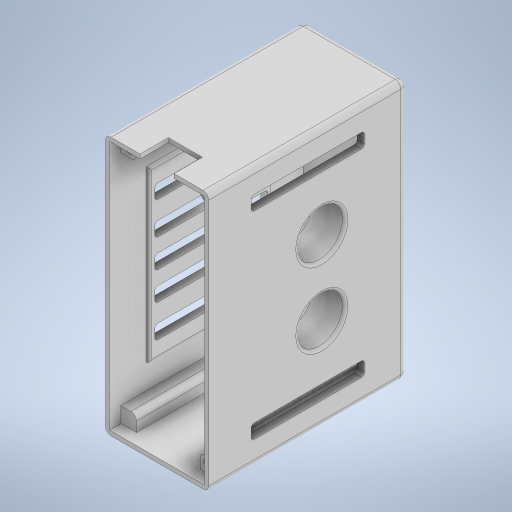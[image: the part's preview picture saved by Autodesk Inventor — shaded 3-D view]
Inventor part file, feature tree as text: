
AUTODESK INVENTOR PART (.ipt)
format: ipt  version: 2024 (Build 280153000, 153)  size: 593,920 bytes
history: native  units: mm
features: extrude x13, sketch x13, fillet x11
ambient origin geometry x8: Origin, YZ Plane, XZ Plane, XY Plane, X Axis, Y Axis, Z Axis, Center Point
bodies: Volumenkörper1 (feature_tree)
feature tree (37):
  extrude  "Extrusion1"  Depth=36.6mm
  extrude  "Extrusion2"  Depth=1.5mm
  extrude  "Extrusion3"  Depth=1.5mm
  extrude  "Extrusion5"  Depth=68.5mm TaperAngle=0.0deg
  fillet  "Rundung2"  Radius=30.0mm
  extrude  "Extrusion9"  Depth=16.5mm
  extrude  "Extrusion11"  Depth=2.0mm TaperAngle=0.0deg
  extrude  "Extrusion12"  Depth=18.0mm
  sketch  "Skizze15"  dims[d50=5.5mm d51=5.5mm d55=5.5mm]
  sketch  "Skizze16"  dims[d56=5.5mm d57=5.5mm]
  fillet  "Rundung5"  Radius=11.0mm
  fillet  "Rundung6"  Radius=1.0mm
  extrude  "Extrusion17"  Depth=5.5mm
  sketch  "Skizze24"  dims[d71=2.5mm d72=15.0mm d73=0.0mm d74=10.0mm d75=12.0mm d76=4.0mm d77=0.0mm d85=11.5mm d86=10.0mm]
  fillet  "Rundung7"  Radius=5.5mm
  extrude  "Extrusion21"  Depth=5.5mm
  extrude  "Extrusion23"  Depth=2.5mm
  extrude  "Extrusion24"  Depth=15.0mm TaperAngle=0.0deg
  fillet  "Rundung8"  Radius=10.0mm
  fillet  "Rundung9"  Radius=12.0mm
  fillet  "Rundung10"  Radius=4.0mm
  fillet  "Rundung11"  Radius=11.5mm
  fillet  "Rundung12"  Radius=10.0mm
  extrude  "Extrusion26"  Depth=5.0mm
  fillet  "Rundung13"  Radius=5.0mm
  extrude  "Extrusion27"  Depth=5.0mm
  fillet  "Rundung14"  Radius=5.0mm
  sketch  "Skizze1"  dims[d0=91.5mm d1=36.6mm]
  sketch  "Skizze2"  dims[d2=70.0mm d3=0.0mm d4=1.5mm]
  sketch  "Skizze3"  dims[d5=1.5mm d6=1.5mm]
  sketch  "Skizze5"  dims[d7=1.5mm d8=68.5mm d9=0.0mm d10=30.0mm]
  sketch  "Skizze10"  dims[d11=16.5mm d12=16.5mm]
  sketch  "Skizze13"  dims[d13=26.5mm d14=2.0mm d15=0.0mm]
  sketch  "Skizze14"  dims[d18=18.0mm d19=18.0mm d20=11.0mm d21=0.0mm d49=1.0mm]
  sketch  "Skizze19"  dims[d58=64.5mm d59=0.0mm d70=2.5mm]
  sketch  "Skizze28"  dims[d87=11.5mm d88=5.0mm d89=5.0mm]
  sketch  "Skizze30"  dims[d90=5.0mm d91=5.0mm d92=5.0mm d93=40.0mm d94=10.0mm d98=5.0mm d99=5.0mm d100=40.0mm d101=70.0mm d105=2.0mm d106=2.0mm d111=45.0mm d112=20.5mm d114=12.0mm d116=5.0mm d118=5.0mm d119=5.0mm d120=5.0mm d121=12.0mm d122=16.5mm d123=2.0mm d124=11.0mm d125=0.0mm d126=9.25mm d127=3.1mm d128=3.1mm d129=3.1mm d130=3.1mm d149=1.5mm d150=1.5mm d151=1.5mm d152=1.5mm d153=1.5mm d154=1.5mm d155=1.5mm d156=1.5mm d157=1.5mm d158=1.5mm d159=1.5mm d160=1.5mm d161=1.0mm d162=5.0mm d163=0.0mm d175=22.0mm d176=30.0mm d177=1.0mm d178=0.0mm d179=7.0mm d180=0.0mm d181=1.0mm d182=1.0mm d183=1.0mm d184=1.0mm d185=1.0mm d190=7.5mm d191=44.0mm d192=44.0mm d193=13.0mm d194=1.0mm d195=0.0mm d196=1.0mm d197=3.0mm d198=0.0mm d199=1.0mm]
